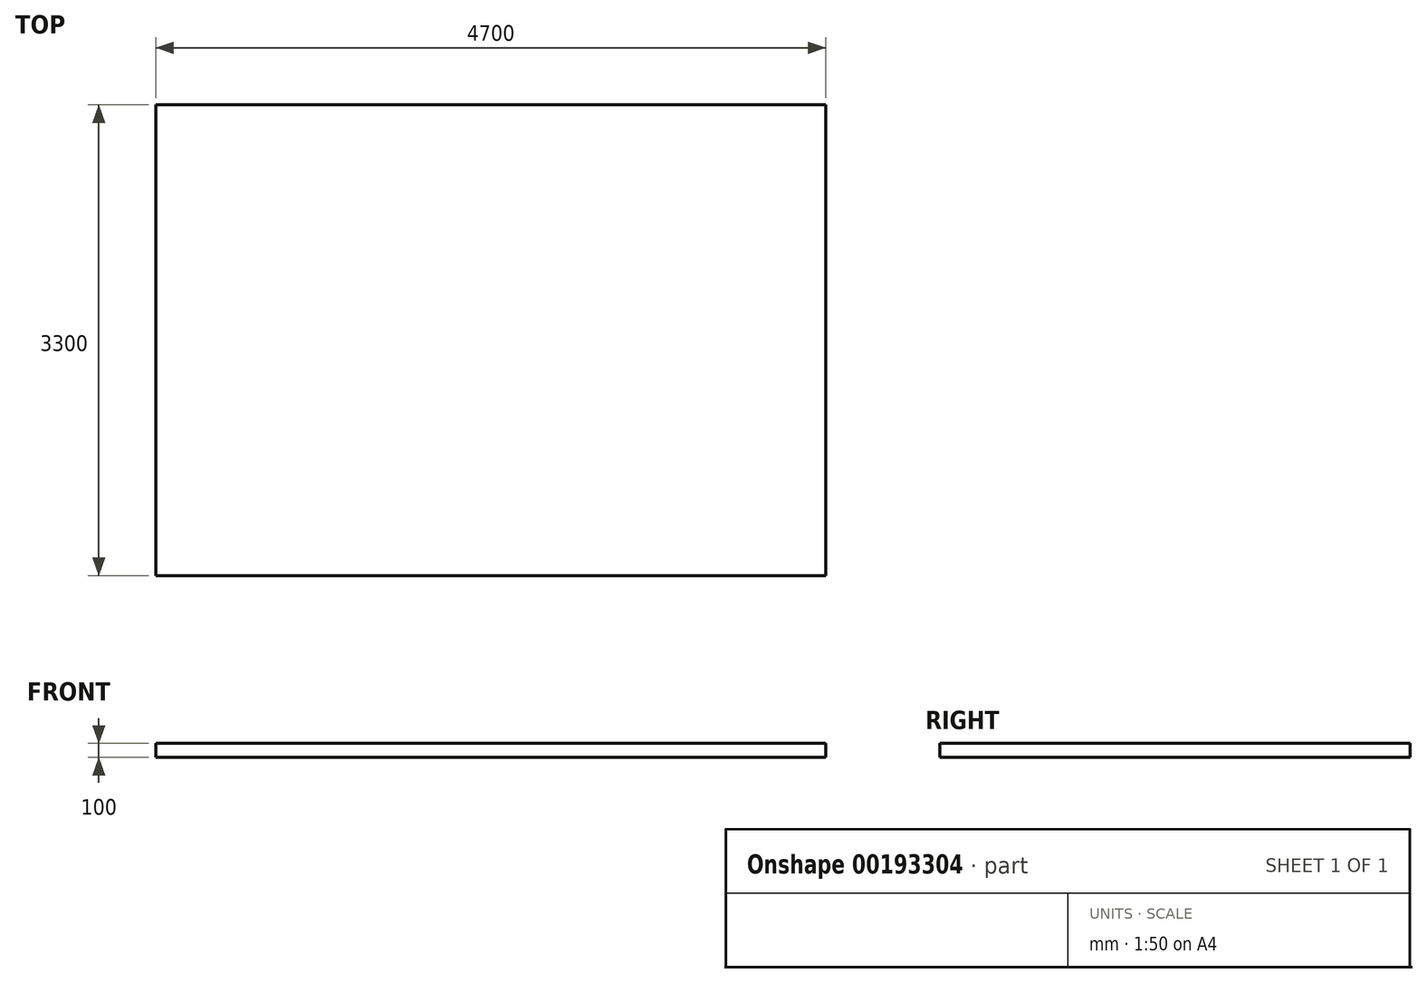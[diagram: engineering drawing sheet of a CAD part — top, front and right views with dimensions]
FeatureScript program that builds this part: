
annotation { "Feature Type Name" : "Feature", "Feature Type Description" : "" }
export const myFeature = defineFeature(function(context is Context, id is Id, definition is map)
    precondition{}
    {
        {
            var Q0;
            Q0=qCreatedBy(makeId("Top.planeOp"),FACE);
            var sketch = newSketch(context, id + "F0", { "sketchPlane" : qUnion([Q0])});
            skLineSegment(sketch, "E0.bottom", {"start": v(-2388.86, 1576.38) * mm, "end": v(2311.14, 1576.38) * mm});
            skLineSegment(sketch, "E0.top", {"start": v(-2388.86, -1723.62) * mm, "end": v(2311.14, -1723.62) * mm});
            skLineSegment(sketch, "E0.left", {"start": v(-2388.86, 1576.38) * mm, "end": v(-2388.86, -1723.62) * mm});
            skLineSegment(sketch, "E0.right", {"start": v(2311.14, 1576.38) * mm, "end": v(2311.14, -1723.62) * mm});
            skSolve(sketch);
        }
        {
            var Q0;
            Q0=qSketchRegion(id+"F0",true);
            extrude(context, id + "F1", {"entities" : qUnion([Q0]), "depth" : 100 * mm});
        }
    });
